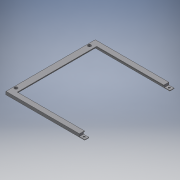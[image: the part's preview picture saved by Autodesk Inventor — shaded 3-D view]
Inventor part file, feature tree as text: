
AUTODESK INVENTOR PART (.ipt)
format: ipt  version: 2016 SP2 (Build 200236200, 236)  size: 132,608 bytes
history: native  units: mm
features: sketch x5, other x3
ambient origin geometry x8: Origin, YZ Plane, XZ Plane, XY Plane, X Axis, Y Axis, Z Axis, Center Point
bodies: Volumenkörper1 (feature_tree)
feature tree (8):
  other  "Case-Side.ipt"
  other  "Volumenkörper1::Case-Side.ipt"
  other  "Bezeichnung1"
  sketch  "Skizze1"  dims[d0=10.0mm]
  sketch  "Skizze2"
  sketch  "Skizze3"
  sketch  "Skizze4"
  sketch  "Skizze5"
